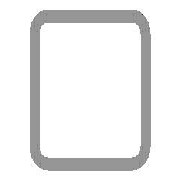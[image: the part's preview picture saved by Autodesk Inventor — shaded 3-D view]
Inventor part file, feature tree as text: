
AUTODESK INVENTOR PART (.ipt)
format: ipt  version: 2025 (Build 290162010, 162A)  size: 133,120 bytes
history: native  units: mm (DEFAULTED — no unit token found)
features: other x4, sketch x1, plane x1
ambient origin geometry x8: Origin, YZ Plane, XZ Plane, XY Plane, X Axis, Y Axis, Z Axis, Center Point
bodies: Solid1 (feature_tree), Body (feature_tree)
feature tree (6):
  parser-record x1  (decoder bookkeeping rows leaked as tree rows — omitted from the tree; the rows remain in map.json)
  other  "Driven Length"
  other  "Start plane"
  other  "End plane"
  sketch  "Sketch3"  dims[d3=7000.0mm d4=0.0mm d7=6.0mm d9=80.0mm d11=80.0mm d12=3.0mm d13=-0.0mm d14=7000.0mm d15=40.0mm d16=40.0mm d17=90.0deg d18=7000.0mm]
  plane  "Work Plane3"
